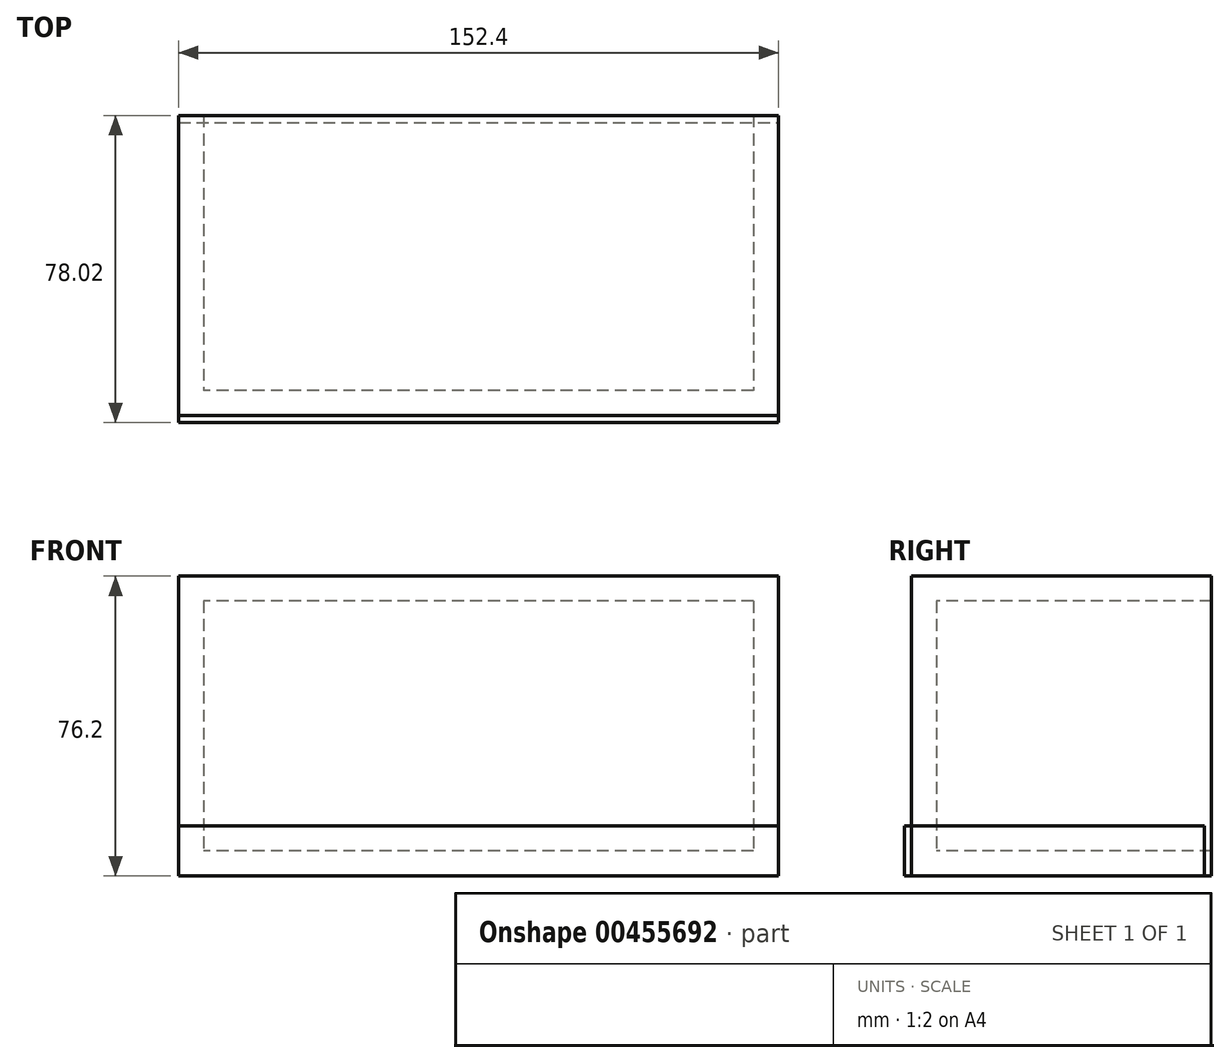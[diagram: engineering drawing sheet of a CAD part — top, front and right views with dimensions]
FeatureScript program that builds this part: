
annotation { "Feature Type Name" : "Feature", "Feature Type Description" : "" }
export const myFeature = defineFeature(function(context is Context, id is Id, definition is map)
    precondition{}
    {
        {
            var Q0;
            Q0=qCreatedBy(makeId("Top.planeOp"),FACE);
            var sketch = newSketch(context, id + "F0", { "sketchPlane" : qUnion([Q0])});
            skLineSegment(sketch, "E0.bottom", {"start": v(76.2, 38.1) * mm, "end": v(-76.2, 38.1) * mm});
            skLineSegment(sketch, "E0.top", {"start": v(76.2, -38.1) * mm, "end": v(-76.2, -38.1) * mm});
            skLineSegment(sketch, "E0.left", {"start": v(76.2, 38.1) * mm, "end": v(76.2, -38.1) * mm});
            skLineSegment(sketch, "E0.right", {"start": v(-76.2, 38.1) * mm, "end": v(-76.2, -38.1) * mm});
            skPoint(sketch, "E0.middle", {"position": v(0, 0) * mm});
            skSolve(sketch);
        }
        {
            var Q0;
            Q0 = qSketchRegion(id + "F0", true);
            extrude(context, id + "F1", {"entities" : qUnion([Q0]), "depth" : 76.2 * mm});
        }
        {
            var Q0;
            Q0=makeQuery(id+"F1.opExtrude","SWEPT_FACE",FACE,{"disambiguationData":[OSD([sQuery(id+"F0.wireOp",EDGE,"E0.bottom")])]});
            shell(context, id + "F2", {"entities" : qUnion([Q0]), "thickness" : 6.35 * mm});
        }
        {
            var Q0;
            Q0=qCreatedBy(makeId("Top.planeOp"),FACE);
            var sketch = newSketch(context, id + "F3", { "sketchPlane" : qUnion([Q0])});
            skLineSegment(sketch, "E1.bottom", {"start": v(-76.2, -39.92) * mm, "end": v(76.2, -39.92) * mm});
            skLineSegment(sketch, "E1.top", {"start": v(-76.2, 36.28) * mm, "end": v(76.2, 36.28) * mm});
            skLineSegment(sketch, "E1.left", {"start": v(-76.2, -39.92) * mm, "end": v(-76.2, 36.28) * mm});
            skLineSegment(sketch, "E1.right", {"start": v(76.2, -39.92) * mm, "end": v(76.2, 36.28) * mm});
            skPoint(sketch, "E1.middle", {"position": v(0, -1.82) * mm});
            skSolve(sketch);
        }
        {
            var Q0;
            Q0 = qSketchRegion(id + "F3", true);
            extrude(context, id + "F4", {"entities" : qUnion([Q0]), "depth" : 12.7 * mm});
        }
    });
